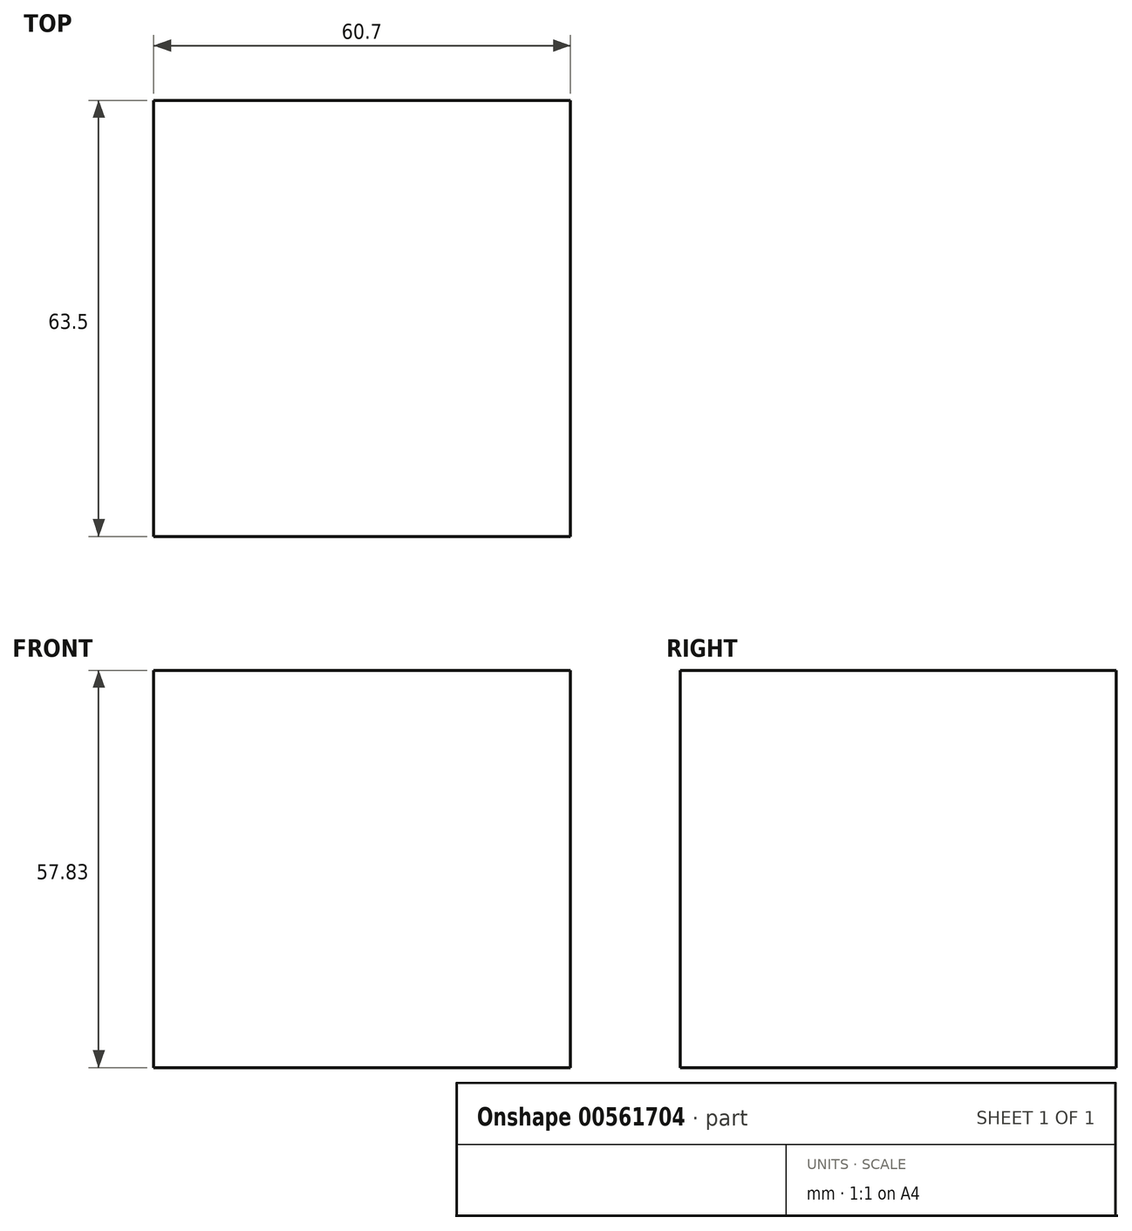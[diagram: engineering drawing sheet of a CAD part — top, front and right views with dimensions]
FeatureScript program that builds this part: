
annotation { "Feature Type Name" : "Feature", "Feature Type Description" : "" }
export const myFeature = defineFeature(function(context is Context, id is Id, definition is map)
    precondition{}
    {
        {
            var Q0;
            Q0=qCreatedBy(makeId("Front.planeOp"),FACE);
            var sketch = newSketch(context, id + "F0", { "sketchPlane" : qUnion([Q0])});
            skLineSegment(sketch, "E0.bottom", {"start": v(0, 0) * mm, "end": v(60.7, 0) * mm});
            skLineSegment(sketch, "E0.top", {"start": v(0, 57.83) * mm, "end": v(60.7, 57.83) * mm});
            skLineSegment(sketch, "E0.left", {"start": v(0, 0) * mm, "end": v(0, 57.83) * mm});
            skLineSegment(sketch, "E0.right", {"start": v(60.7, 0) * mm, "end": v(60.7, 57.83) * mm});
            skSolve(sketch);
        }
        {
            var Q0;
            Q0=makeQuery(id+"F0.imprint","IMPRINT",FACE,{"disambiguationData":[TD([[makeQuery(id+"F0.imprint","IMPRINT",EDGE,{"derivedFrom":sQuery(id+"F0.wireOp",EDGE,"E0.bottom")}),1.0]])]});
            extrude(context, id + "F1", {"entities" : qUnion([Q0]), "depth" : 63.5 * mm, "offsetDistance" : 25.4 * mm});
        }
    });
